# Revit family: IS_Connect_E5671_BIM_DE
name_source: partatom
category: Plumbing Fixtures
revit_build: Autodesk Revit 2016 (Build: 20150220_1215(x64)
units: mm (PartAtom-declared; Revit-internal decimal feet)

## family parameters
Always vertical = No
Cut with Voids When Loaded = No
OmniClass Number = 23.45.05.21.11.21
OmniClass Title = Urinals
Part Type = Normal
Room Calculation Point = No
Round Connector Dimension = Use Diameter
Shared = No
Work Plane-Based = No

## types (1)
- E567101 - CONNECT ORINATOIO ALIM POSTERIORE
    Accessories = www.idealstandard.de\ersatzteile
    AreaUnits = millimeters
    Assembly Code = C1030206
    AssetType = Fixed
    BIMObjectName = ISI_IdealStandard_Urinals_CONNECT_E567101
    BIMobject category = Urinals
    BOSUseNativeGeometries = 1
    BarCode = 5017830480495
    Brand url = http://www.idealstandard.co.uk
    CodePerformance = DIN EN 13407 CL1 - I - 2C, DIN EN
    Color = White
    ConnectionType = Plumbing
    Cost = 0 $
    CurrencyUnit = €
    Date of publishing = 4/3/2017
    Description = CONNECT - Orinatoio sospeso 57x31 cm. con alimentazione posteriore, completo di fissaggi scarico a scelta orizzontale nascosto o verticale a vista.
    DurationUnit = year
    EAN code = https://5017830480495
    Edition number = 1
    ExpectedLife = 25
    Features = CONNECT urinal 310x335mm, back inlet
    Finish = White
    GrossWeight = 13 kg
    IFC Classification = Sanitary Terminal
    Installation instructions = http://www.idealstandard.de
    InstallationDate = 1900-12-31T23:59:59
    InstallationInstructions = www.idealstandard.de\produkte
    LinearUnits = millimeters
    Manufacturer name = Ideal Standard
    ManufacturerURL = www.idealstandard.de
    Material = Vitreous china
    Material main = Ceramics
    Model = E567101
    ModelNumber = E567101
    ModelReference = IS Absaugeurinal CONNECT, Zulauf v.hi., 310x335x570mm, Weiß
    Name = ISI_IdealStandard_Urinals_CONNECT_E567101
    Nominal height = 570
    Nominal width = 310
    NominalDepth = 0 mm  [stored 0 ft]
    NominalLength = 337 mm
    OmniClass Code = 23-31 21 00
    OmniClass Description = Urinals
    Product Guid = 3c019878-5d0d-4ab9-b919-00e32e3b589f
    Product SKU = E5671
    Product data url = https://bimobject.com
    Product family = CONNECT
    Product group = Urinal
    Product url = http://www.idealstandard.de
    ProductInformation = www.idealstandard.de
    ProfonditaNominale = 0
    QR code = http://bimobject.com
    Shape = Sculptured
    Size = 310 x 337 x 571 mm
    Space = Internal
    Technical description = http://www.idealstandard.de
    URL = www.idealstandard.de
    Uniclass 2015 Code = Pr_40_20_93_82
    Uniclass 2015 Name = Wall-hung urinals
    Uniclass2015Code = Pr_40_20_93_82
    Uniclass2015Title = Wall hung urinals
    Uniclass2015Version = Products v1.1
    Version = 1
    VolumeUnits = Litres
    Weight Net (Kg) = 13

note: [stored X ft] marks values corroborated as IEEE doubles in the binary element streams (Revit-internal decimal feet)

## geometry (parser evidence)
native form markers: Blend x2, Sweep x3
no freeform markers — native parametric forms only
